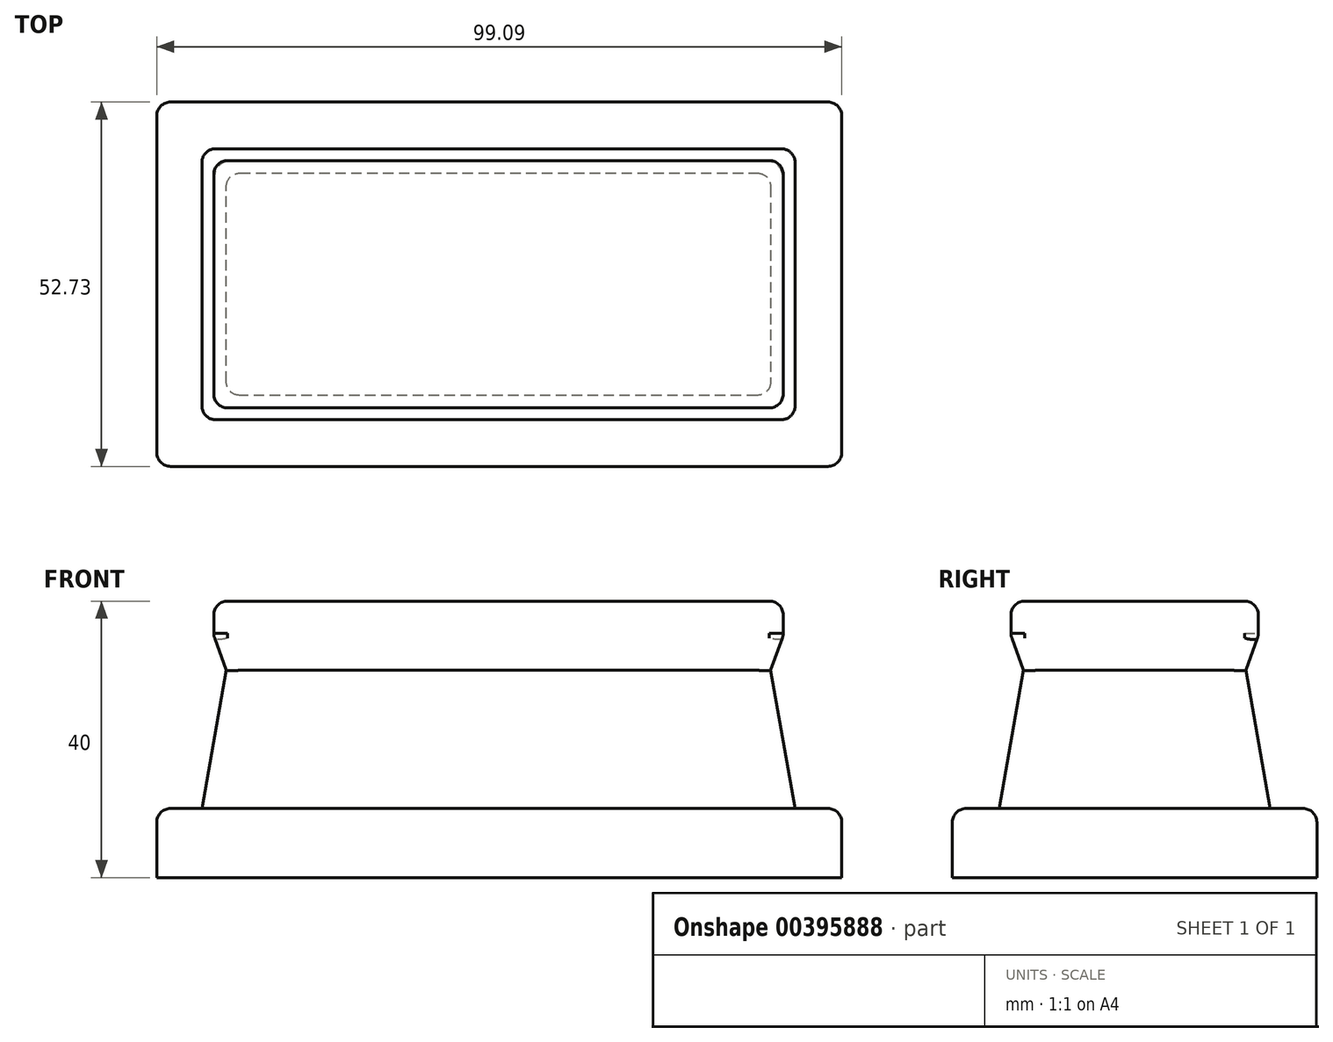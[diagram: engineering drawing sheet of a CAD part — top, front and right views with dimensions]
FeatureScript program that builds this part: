
annotation { "Feature Type Name" : "Feature", "Feature Type Description" : "" }
export const myFeature = defineFeature(function(context is Context, id is Id, definition is map)
    precondition{}
    {
        {
            var Q0;
            Q0=qCreatedBy(makeId("Top.planeOp"),FACE);
            var sketch = newSketch(context, id + "F0", { "sketchPlane" : qUnion([Q0])});
            skLineSegment(sketch, "E0.bottom", {"start": v(-48.04, 32) * mm, "end": v(51.05, 32) * mm});
            skLineSegment(sketch, "E0.top", {"start": v(-48.04, -20.73) * mm, "end": v(51.05, -20.73) * mm});
            skLineSegment(sketch, "E0.left", {"start": v(-48.04, 32) * mm, "end": v(-48.04, -20.73) * mm});
            skLineSegment(sketch, "E0.right", {"start": v(51.05, 32) * mm, "end": v(51.05, -20.73) * mm});
            skLineSegment(sketch, "E1.bottom", {"start": v(-43.27, 27) * mm, "end": v(46.05, 27) * mm});
            skLineSegment(sketch, "E1.top", {"start": v(-43.27, -15.73) * mm, "end": v(46.05, -15.73) * mm});
            skLineSegment(sketch, "E1.left", {"start": v(-43.27, 27) * mm, "end": v(-43.27, -15.73) * mm});
            skLineSegment(sketch, "E1.right", {"start": v(46.05, 27) * mm, "end": v(46.05, -15.73) * mm});
            skSolve(sketch);
        }
        {
            var Q0;
            Q0=makeQuery(id+"F0.imprint","IMPRINT",FACE,{"disambiguationData":[TD([[makeQuery(id+"F0.imprint","IMPRINT",EDGE,{"derivedFrom":sQuery(id+"F0.wireOp",EDGE,"E0.bottom")}),-1.0]])]});
            var Q1;
            Q1=makeQuery(id+"F0.imprint","IMPRINT",FACE,{"disambiguationData":[TD([[makeQuery(id+"F0.imprint","IMPRINT",EDGE,{"derivedFrom":sQuery(id+"F0.wireOp",EDGE,"E1.bottom")}),-1.0]])]});
            extrude(context, id + "F1", {"entities" : qUnion([Q0, Q1]), "depth" : 10 * mm});
        }
        {
            var Q0;
            Q0=makeQuery(id+"F0.imprint","IMPRINT",FACE,{"disambiguationData":[TD([[makeQuery(id+"F0.imprint","IMPRINT",EDGE,{"derivedFrom":sQuery(id+"F0.wireOp",EDGE,"E1.bottom")}),-1.0]])]});
            extrude(context, id + "F2", {"entities" : qUnion([Q0]), "operationType" : NewBodyOperationType.ADD, "depth" : 30 * mm, "hasDraft" : true, "draftAngle" : 10 * degree, "draftPullDirection" : true});
        }
        {
            var Q0;
            Q0=makeQuery(id+"F2.opExtrude","CAP_FACE",FACE,{"disambiguationData":[OSD([sQuery(id+"F0.wireOp",EDGE,"E1.bottom"),sQuery(id+"F0.wireOp",EDGE,"E1.top"),sQuery(id+"F0.wireOp",EDGE,"E1.left"),sQuery(id+"F0.wireOp",EDGE,"E1.right")])],"isStart":false});
            extrude(context, id + "F3", {"entities" : qUnion([Q0]), "operationType" : NewBodyOperationType.ADD, "depth" : 5 * mm, "hasDraft" : true, "draftAngle" : 20 * degree});
        }
        {
            var Q0;
            Q0=makeQuery(id+"F3.opExtrude","CAP_FACE",FACE,{"disambiguationData":[OSD([sQuery(id+"F0.wireOp",EDGE,"E1.bottom"),sQuery(id+"F0.wireOp",EDGE,"E1.top"),sQuery(id+"F0.wireOp",EDGE,"E1.left"),sQuery(id+"F0.wireOp",EDGE,"E1.right")])],"isStart":false});
            extrude(context, id + "F4", {"entities" : qUnion([Q0]), "operationType" : NewBodyOperationType.ADD, "depth" : 5 * mm});
        }
        {
            var Q0;
            Q0=makeQuery(id+"F4.opExtrude","CAP_EDGE",EDGE,{"disambiguationData":[OSD([sQuery(id+"F0.wireOp",EDGE,"E1.top")])],"isStart":false});
            var Q1;
            Q1=makeQuery(id+"F4.opExtrude","CAP_EDGE",EDGE,{"disambiguationData":[OSD([sQuery(id+"F0.wireOp",EDGE,"E1.bottom")])],"isStart":false});
            var Q2;
            Q2=makeQuery(id+"F4.opExtrude","CAP_EDGE",EDGE,{"disambiguationData":[OSD([sQuery(id+"F0.wireOp",EDGE,"E1.right")])],"isStart":false});
            var Q3;
            Q3=makeQuery(id+"F4.opExtrude","CAP_EDGE",EDGE,{"disambiguationData":[OSD([sQuery(id+"F0.wireOp",EDGE,"E1.left")])],"isStart":false});
            var Q4;
            Q4=makeQuery(id+"F4.opExtrude","SWEPT_EDGE",EDGE,{"disambiguationData":[OSD([sQuery(id+"F0.wireOp",EDGE,"E1.top"),sQuery(id+"F0.wireOp",EDGE,"E1.right")])]});
            var Q5;
            {var subQ0=sQuery(id+"F0.wireOp",EDGE,"E1.top");Q5=makeQuery(id+"F4.boolean.opBoolean","MERGE",EDGE,{"derivedFrom":[makeQuery(id+"F3.opExtrude","CAP_EDGE",EDGE,{"disambiguationData":[OSD([subQ0])],"isStart":false}),makeQuery(id+"F4.opExtrude","CAP_EDGE",EDGE,{"disambiguationData":[OSD([subQ0])],"isStart":true})]});}
            var Q6;
            {var subQ0=sQuery(id+"F0.wireOp",EDGE,"E1.right");Q6=makeQuery(id+"F4.boolean.opBoolean","MERGE",EDGE,{"derivedFrom":[makeQuery(id+"F3.opExtrude","CAP_EDGE",EDGE,{"disambiguationData":[OSD([subQ0])],"isStart":false}),makeQuery(id+"F4.opExtrude","CAP_EDGE",EDGE,{"disambiguationData":[OSD([subQ0])],"isStart":true})]});}
            var Q7;
            {var subQ0=sQuery(id+"F0.wireOp",EDGE,"E1.bottom");Q7=makeQuery(id+"F4.boolean.opBoolean","MERGE",EDGE,{"derivedFrom":[makeQuery(id+"F3.opExtrude","CAP_EDGE",EDGE,{"disambiguationData":[OSD([subQ0])],"isStart":false}),makeQuery(id+"F4.opExtrude","CAP_EDGE",EDGE,{"disambiguationData":[OSD([subQ0])],"isStart":true})]});}
            var Q8;
            Q8=makeQuery(id+"F4.opExtrude","SWEPT_EDGE",EDGE,{"disambiguationData":[OSD([sQuery(id+"F0.wireOp",EDGE,"E1.bottom"),sQuery(id+"F0.wireOp",EDGE,"E1.right")])]});
            var Q9;
            Q9=makeQuery(id+"F4.opExtrude","SWEPT_EDGE",EDGE,{"disambiguationData":[OSD([sQuery(id+"F0.wireOp",EDGE,"E1.bottom"),sQuery(id+"F0.wireOp",EDGE,"E1.left")])]});
            var Q10;
            Q10=makeQuery(id+"F4.opExtrude","SWEPT_EDGE",EDGE,{"disambiguationData":[OSD([sQuery(id+"F0.wireOp",EDGE,"E1.top"),sQuery(id+"F0.wireOp",EDGE,"E1.left")])]});
            var Q11;
            {var subQ0=sQuery(id+"F0.wireOp",EDGE,"E1.left");Q11=makeQuery(id+"F4.boolean.opBoolean","MERGE",EDGE,{"derivedFrom":[makeQuery(id+"F3.opExtrude","CAP_EDGE",EDGE,{"disambiguationData":[OSD([subQ0])],"isStart":false}),makeQuery(id+"F4.opExtrude","CAP_EDGE",EDGE,{"disambiguationData":[OSD([subQ0])],"isStart":true})]});}
            var Q12;
            Q12=makeQuery(id+"F3.opExtrude","SWEPT_EDGE",EDGE,{"disambiguationData":[OSD([sQuery(id+"F0.wireOp",EDGE,"E1.top"),sQuery(id+"F0.wireOp",EDGE,"E1.left")])]});
            var Q13;
            Q13=makeQuery(id+"F3.opExtrude","SWEPT_EDGE",EDGE,{"disambiguationData":[OSD([sQuery(id+"F0.wireOp",EDGE,"E1.bottom"),sQuery(id+"F0.wireOp",EDGE,"E1.left")])]});
            var Q14;
            Q14=makeQuery(id+"F3.opExtrude","SWEPT_EDGE",EDGE,{"disambiguationData":[OSD([sQuery(id+"F0.wireOp",EDGE,"E1.top"),sQuery(id+"F0.wireOp",EDGE,"E1.right")])]});
            var Q15;
            Q15=makeQuery(id+"F3.opExtrude","SWEPT_EDGE",EDGE,{"disambiguationData":[OSD([sQuery(id+"F0.wireOp",EDGE,"E1.bottom"),sQuery(id+"F0.wireOp",EDGE,"E1.right")])]});
            var Q16;
            Q16=makeQuery(id+"F2.opExtrude","SWEPT_EDGE",EDGE,{"disambiguationData":[OSD([sQuery(id+"F0.wireOp",EDGE,"E1.bottom"),sQuery(id+"F0.wireOp",EDGE,"E1.right")])]});
            var Q17;
            Q17=makeQuery(id+"F2.opExtrude","SWEPT_EDGE",EDGE,{"disambiguationData":[OSD([sQuery(id+"F0.wireOp",EDGE,"E1.top"),sQuery(id+"F0.wireOp",EDGE,"E1.right")])]});
            var Q18;
            Q18=makeQuery(id+"F2.opExtrude","SWEPT_EDGE",EDGE,{"disambiguationData":[OSD([sQuery(id+"F0.wireOp",EDGE,"E1.top"),sQuery(id+"F0.wireOp",EDGE,"E1.left")])]});
            var Q19;
            Q19=makeQuery(id+"F2.opExtrude","SWEPT_EDGE",EDGE,{"disambiguationData":[OSD([sQuery(id+"F0.wireOp",EDGE,"E1.bottom"),sQuery(id+"F0.wireOp",EDGE,"E1.left")])]});
            var Q20;
            Q20=makeQuery(id+"F1.opExtrude","CAP_EDGE",EDGE,{"disambiguationData":[OSD([sQuery(id+"F0.wireOp",EDGE,"E0.top")])],"isStart":false});
            var Q21;
            Q21=makeQuery(id+"F1.opExtrude","CAP_EDGE",EDGE,{"disambiguationData":[OSD([sQuery(id+"F0.wireOp",EDGE,"E0.left")])],"isStart":false});
            var Q22;
            Q22=makeQuery(id+"F1.opExtrude","CAP_EDGE",EDGE,{"disambiguationData":[OSD([sQuery(id+"F0.wireOp",EDGE,"E0.bottom")])],"isStart":false});
            var Q23;
            Q23=makeQuery(id+"F1.opExtrude","CAP_EDGE",EDGE,{"disambiguationData":[OSD([sQuery(id+"F0.wireOp",EDGE,"E0.right")])],"isStart":false});
            fillet(context, id + "F5", {"entities" : qUnion([Q0, Q1, Q2, Q3, Q4, Q5, Q6, Q7, Q8, Q9, Q10, Q11, Q12, Q13, Q14, Q15, Q16, Q17, Q18, Q19, Q20, Q21, Q22, Q23]), "radius" : 2 * mm, "tangentPropagation" : true, "allowEdgeOverflow" : false});
        }
        {
            var Q0;
            Q0=makeQuery(id+"F1.opExtrude","SWEPT_EDGE",EDGE,{"disambiguationData":[OSD([sQuery(id+"F0.wireOp",EDGE,"E0.top"),sQuery(id+"F0.wireOp",EDGE,"E0.right")])]});
            var Q1;
            Q1=makeQuery(id+"F1.opExtrude","SWEPT_EDGE",EDGE,{"disambiguationData":[OSD([sQuery(id+"F0.wireOp",EDGE,"E0.bottom"),sQuery(id+"F0.wireOp",EDGE,"E0.right")])]});
            var Q2;
            Q2=makeQuery(id+"F1.opExtrude","SWEPT_EDGE",EDGE,{"disambiguationData":[OSD([sQuery(id+"F0.wireOp",EDGE,"E0.top"),sQuery(id+"F0.wireOp",EDGE,"E0.left")])]});
            var Q3;
            Q3=makeQuery(id+"F1.opExtrude","SWEPT_EDGE",EDGE,{"disambiguationData":[OSD([sQuery(id+"F0.wireOp",EDGE,"E0.bottom"),sQuery(id+"F0.wireOp",EDGE,"E0.left")])]});
            fillet(context, id + "F6", {"entities" : qUnion([Q0, Q1, Q2, Q3]), "radius" : 2 * mm, "tangentPropagation" : true, "allowEdgeOverflow" : false});
        }
    });
